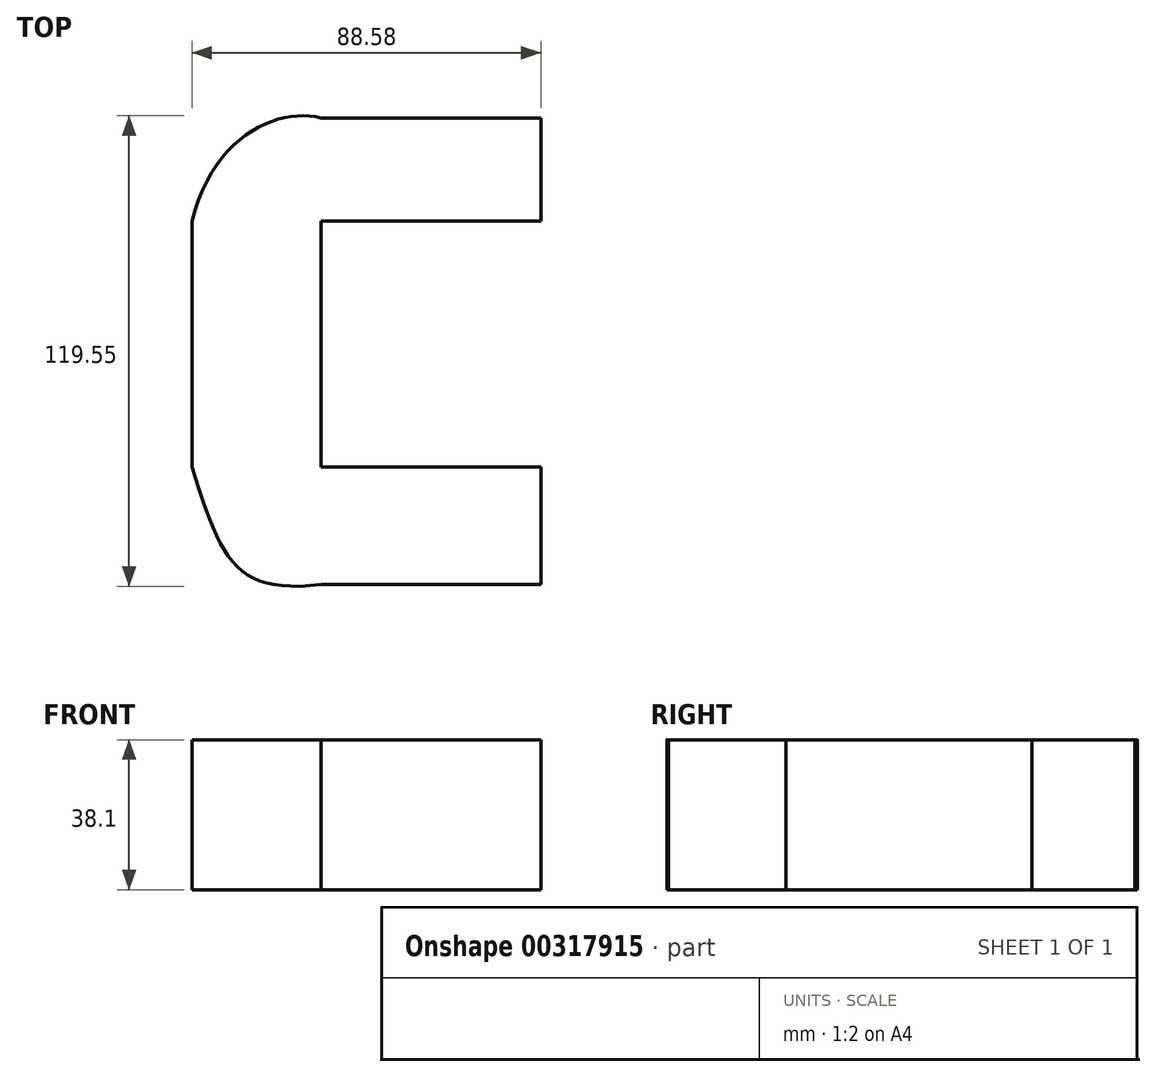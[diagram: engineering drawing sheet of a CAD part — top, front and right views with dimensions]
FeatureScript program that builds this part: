
annotation { "Feature Type Name" : "Feature", "Feature Type Description" : "" }
export const myFeature = defineFeature(function(context is Context, id is Id, definition is map)
    precondition{}
    {
        {
            var Q0;
            Q0=qCreatedBy(makeId("Top.planeOp"),FACE);
            var sketch = newSketch(context, id + "F0", { "sketchPlane" : qUnion([Q0])});
            skLineSegment(sketch, "E0.bottom", {"start": v(-22.04, 25.43) * mm, "end": v(10.7, 25.43) * mm});
            skLineSegment(sketch, "E0.top", {"start": v(-22.04, -37.08) * mm, "end": v(10.7, -37.08) * mm});
            skLineSegment(sketch, "E0.left", {"start": v(-22.04, 25.43) * mm, "end": v(-22.04, -37.08) * mm});
            skLineSegment(sketch, "E0.right", {"start": v(10.7, 25.43) * mm, "end": v(10.7, -37.08) * mm});
            skLineSegment(sketch, "E1.bottom", {"start": v(10.7, -37.08) * mm, "end": v(66.54, -37.08) * mm});
            skLineSegment(sketch, "E1.top", {"start": v(10.7, -66.96) * mm, "end": v(66.54, -66.96) * mm});
            skLineSegment(sketch, "E1.left", {"start": v(10.7, -37.08) * mm, "end": v(10.7, -66.96) * mm});
            skLineSegment(sketch, "E1.right", {"start": v(66.54, -37.08) * mm, "end": v(66.54, -66.96) * mm});
            skLineSegment(sketch, "E2.bottom", {"start": v(10.7, 25.43) * mm, "end": v(66.54, 25.43) * mm});
            skLineSegment(sketch, "E2.top", {"start": v(10.7, 51.6) * mm, "end": v(66.54, 51.6) * mm});
            skLineSegment(sketch, "E2.left", {"start": v(10.7, 25.43) * mm, "end": v(10.7, 51.6) * mm});
            skLineSegment(sketch, "E2.right", {"start": v(66.54, 25.43) * mm, "end": v(66.54, 51.6) * mm});
            skFitSpline(sketch, "E3", {"points": [v(-22.04, -37.08) * mm, v(10.7, -66.96) * mm], "startDerivative": vector(21.61, -69.93) * mm, "endDerivative": vector(66.12, 7.63) * mm});
            skFitSpline(sketch, "E4", {"points": [v(-22.04, 25.43) * mm, v(10.7, 51.6) * mm], "startDerivative": vector(16.53, 66.12) * mm, "endDerivative": vector(32.11, -8.3) * mm});
            skSolve(sketch);
        }
        {
            var Q0;
            Q0 = qSketchRegion(id + "F0", true);
            extrude(context, id + "F1", {"entities" : qUnion([Q0]), "oppositeDirection" : true, "depth" : 38.1 * mm});
        }
    });
